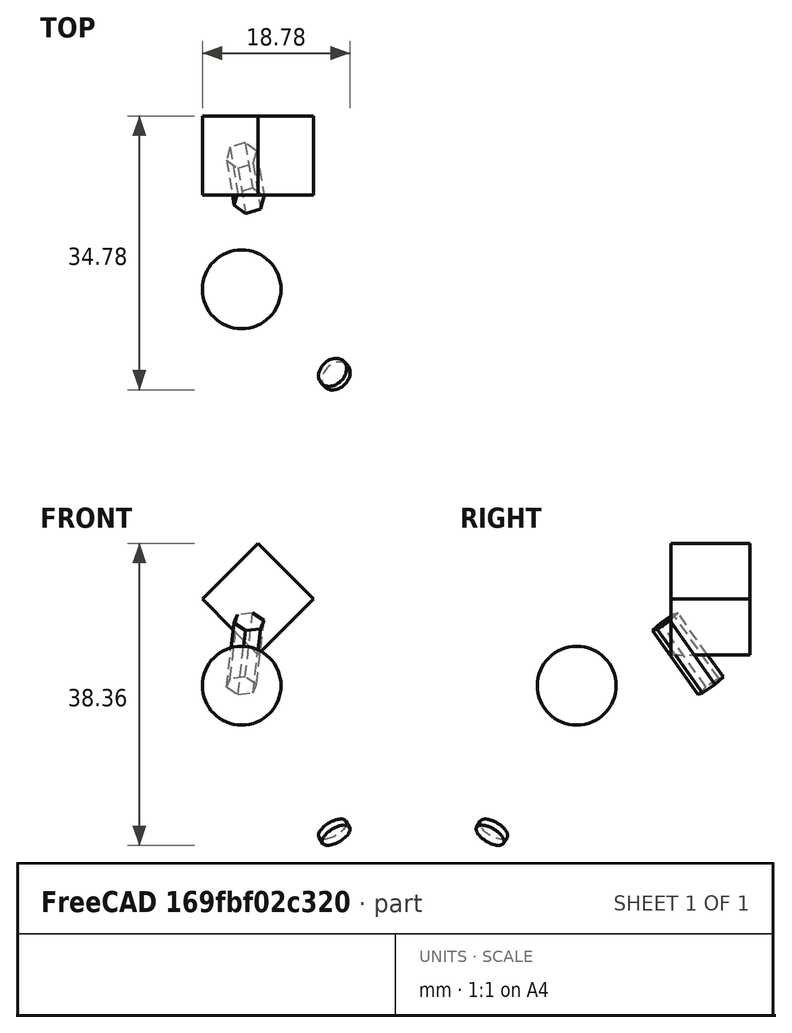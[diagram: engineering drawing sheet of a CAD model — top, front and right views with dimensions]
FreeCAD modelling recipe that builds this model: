
FCSTD DOCUMENT  (FreeCAD 1.1R44874 (Git))
Label: nested-structure
License: All rights reserved
LicenseURL: https://en.wikipedia.org/wiki/All_rights_reserved
objects: App::Point×6, App::LinkGroupPython×5, App::Part×5, App::Link×3, App::DocumentObjectGroup×3, Part::Box×1, Part::Sphere×1, Part::Cylinder×1, Part::FeaturePython×1, PartDesign::AdditivePrism×1, PartDesign::Body×1
note: 8 computed .brp shape members not serialized (recipe doc carries the construction recipe); baked Part::Feature solids carry a one-line shape summary decoded from their .brp
EXTERNAL_REF file=external-file.FCStd obj=Part
EXTERNAL_REF file=external-file.FCStd obj=Part002
EXTERNAL_REF file=external-file2.FCStd obj=Common

FEATURE [App::Link] Link001  label="external-file-mirror"
  LinkPlacement = pos=(0,0,23) rot=(0,1,0;0.785398rad)
  LinkedObject = -> <external external-file.FCStd>#Part
  Placement = pos=(0,0,23) rot=(0,1,0;0.785398rad)
  ShowElement = false
FEATURE [App::LinkGroupPython] OpticalPointSource  label="OpticalPointSource001"  # WARN: FeaturePython — macro-defined, semantics opaque (R4)
  Divergence = -
  FanPhi0 = 0
  Fans = 2
  FocalLength = -100
  LinkMode = 0
  MaxIntersectionsScale = 1
  MaxRayLengthScale = 1
  PhiDomain = 0, 2*pi
  PhiResolutionNumericMode = 100
  Placement = pos=(0,0,-5) rot=(0,0,1;0rad)
  PowerDensity = exp(-theta^2/0.01)
  RadiusDomain = 0, 1.00
  RadiusResolutionNumericMode = 100000
  RandomNumberGeneratorMode = ?
  RaysPerFan = 2000
  RaysPerIterationScale = 1
  RecordRays = false
  ThetaDomain = 0, 0.01
  ThetaResolutionNumericMode = 100000
  Wavelength = 500
FEATURE [Part::Box] Box  label="Cube"
  AttacherType = Attacher::AttachEngine3D
  Height = 10
  Length = 10
  Placement = pos=(-5,-5,11) rot=(0,1,0;0.785398rad)
  Width = 10
FEATURE [App::LinkGroupPython] OpticalMirrorGroup  # WARN: FeaturePython — macro-defined, semantics opaque (R4)
  AbsorptionLength = inf
  ElementList = -> [Box]
  GratingDiffractionOrder = 1
  GratingLinesOrientation = (0,0,1)
  GratingLinesPerMillimeter = 1000
  GratingType = 0
  LinkMode = 0
  ModifyPhiDomain = 0, 2*pi
  ModifyThetaDomain = -pi/2, pi/2
  OpticalType = 0
  Placement = pos=(1,0,-1) rot=(0,0,1;0rad)
  PowerPhiDomain = 0, 2*pi
  PowerThetaDomain = -pi/2, pi/2
  RecordHits = false
  Reflectivity = 1
  RefractiveIndex = 2
FEATURE [App::Link] Link  label="doubly-linked-lens"
  LinkedObject = -> <external external-file.FCStd>#Part002
FEATURE [App::Part] Part
  Group = -> [Link]
  Origin = -> Origin
  Placement = pos=(-17,0,11) rot=(0,0,1;0rad)
FEATURE [App::Point] Origin001
  Role = Origin
FEATURE [App::Link] Link002
  LinkedObject = -> <external external-file2.FCStd>#Common
FEATURE [App::Point] Origin003
  Role = Origin
FEATURE [App::Point] Origin005  label="Origin006"
  Role = Origin
FEATURE [App::Point] Origin007  label="Origin009"
  Role = Origin
FEATURE [App::Point] Origin009  label="Origin011"
  Role = Origin
FEATURE [App::Point] Origin011  label="Origin014"
  Role = Origin
FEATURE [Part::Sphere] Sphere
  Angle1 = -90
  Angle2 = 90
  Angle3 = 360
  AttacherType = Attacher::AttachEngine3D
  Placement = pos=(0,-17,0) rot=(0,0,1;0rad)
  Radius = 5
FEATURE [App::LinkGroupPython] OpticalLensGroup  # WARN: FeaturePython — macro-defined, semantics opaque (R4)
  AbsorptionLength = inf
  ElementList = -> [Link002,Sphere]
  GratingDiffractionOrder = 1
  GratingLinesOrientation = (0,0,1)
  GratingLinesPerMillimeter = 1000
  GratingType = 0
  LinkMode = 0
  ModifyPhiDomain = 0, 2*pi
  ModifyThetaDomain = -pi/2, pi/2
  OpticalType = 1
  PowerPhiDomain = 0, 2*pi
  PowerThetaDomain = -pi/2, pi/2
  RecordHits = false
  Reflectivity = 1
  RefractiveIndex = 1.2
FEATURE [Part::Cylinder] Cylinder
  Angle = 360
  AttacherType = Attacher::AttachEngine3D
  FirstAngle = 0
  Height = 1
  Placement = pos=(12,-28,-19) rot=(1,1,0;-0.698132rad)
  Radius = 2
  SecondAngle = 0
FEATURE [App::LinkGroupPython] OpticalVacuumGroup  label="OpticalAbsorberGroup"  # WARN: FeaturePython — macro-defined, semantics opaque (R4)
  AbsorptionLength = inf
  ElementList = -> [Cylinder]
  GratingDiffractionOrder = 1
  GratingLinesOrientation = (0,0,1)
  GratingLinesPerMillimeter = 1000
  GratingType = 0
  LinkMode = 0
  ModifyPhiDomain = 0, 2*pi
  ModifyThetaDomain = -pi/2, pi/2
  OpticalType = 3
  PowerPhiDomain = 0, 2*pi
  PowerThetaDomain = -pi/2, pi/2
  RecordHits = true
  Reflectivity = 1
  RefractiveIndex = 2
FEATURE [Part::FeaturePython] OpticalSimulationSettings  # WARN: FeaturePython — macro-defined, semantics opaque (R4)
  Active = true
  DistanceTolerance = 1e-06
  EnableStoreSingleShotData = false
  EndAfterHits = inf
  EndAfterIterations = inf
  EndAfterRays = 100
  MaxIntersections = 100
  MaxRayLength = 1000
  RaysPerIteration = 5
  SequentialMode = false
  ShowRaysInContinuousMode = true
  StoreHitFanIndex = false
  StoreHitInitDirection = false
  StoreHitInitPhi = false
  StoreHitInitPoint = false
  StoreHitInitPower = false
  StoreHitInitTheta = false
  StoreHitInitWavelength = false
  StoreHitRayIndex = false
  StoreHitTotalFanCount = false
  StoreHitTotalRaysInFan = false
  WorkerProcessCount = num_cpus
FEATURE [PartDesign::AdditivePrism] Prism001
  AttacherType = Attacher::AttachEngine3D
  Circumradius = 2
  FirstAngle = 0
  Height = 10
  Polygon = 6
  Refine = true
  SecondAngle = 0
  Suppressed = false
FEATURE [PartDesign::Body] Body
  AllowCompound = false
  Group = -> [Prism001]
  Origin = -> Origin002
  Placement = pos=(0,0,0) rot=(2,0,1;0.698132rad)
  Tip = -> Prism001
FEATURE [App::Part] Part001
  Group = -> [Body]
  Origin = -> Origin004
  Placement = pos=(7,-4,-6) rot=(-7,6,-5;0.20944rad)
FEATURE [App::LinkGroupPython] OpticalMirrorGroup001  # WARN: FeaturePython — macro-defined, semantics opaque (R4)
  AbsorptionLength = inf
  ElementList = -> [Part001]
  GratingDiffractionOrder = 1
  GratingLinesOrientation = (0,0,1)
  GratingLinesPerMillimeter = 1000
  GratingType = 0
  LinkMode = 0
  ModifyPhiDomain = 0, 2*pi
  ModifyThetaDomain = -pi/2, pi/2
  OpticalType = 0
  Placement = pos=(0,24,21) rot=(-3,3,1;-0.139626rad)
  PowerPhiDomain = 0, 2*pi
  PowerThetaDomain = -pi/2, pi/2
  RecordHits = false
  Reflectivity = 1
  RefractiveIndex = 2
FEATURE [App::Part] Part004
  Group = -> [OpticalMirrorGroup001]
  Origin = -> Origin010
  Placement = pos=(0,0,0) rot=(-3,1,2;-0.767945rad)
FEATURE [App::DocumentObjectGroup] Group002
  Group = -> [Part004]
FEATURE [App::DocumentObjectGroup] Group001
  Group = -> [Group002]
FEATURE [App::Part] Part003
  Group = -> [Group001,Part004,Group002]
  Origin = -> Origin008
  Placement = pos=(-9,8,6) rot=(0,-2,4;0.314159rad)
FEATURE [App::Part] Part002
  Group = -> [Part003]
  Origin = -> Origin006
  Placement = pos=(-12,-7,-6) rot=(3,1,0;0.069813rad)
FEATURE [App::DocumentObjectGroup] Group  label="deeply-nested"
  Group = -> [Part002]

RESOLVED EXTERNAL PARTS (link-assembly join: the EXTERNAL_REF files above that resolve inside this repo's crawl, each included once):
---- part external-file.FCStd = doc fcstd_b1e3236600b9 ----
FCSTD DOCUMENT  (FreeCAD 1.1R44874 (Git))
Label: external-file
License: All rights reserved
LicenseURL: https://en.wikipedia.org/wiki/All_rights_reserved
objects: App::Point×3, App::Part×3, Part::Cylinder×1, App::LinkGroupPython×1, App::Link×1
note: 1 computed .brp shape members not serialized (recipe doc carries the construction recipe); baked Part::Feature solids carry a one-line shape summary decoded from their .brp
EXTERNAL_REF file=external-file2.FCStd obj=Part

FEATURE [Part::Cylinder] Cylinder
  Angle = 360
  AttacherType = Attacher::AttachEngine3D
  FirstAngle = 0
  Height = 1
  Radius = 2
  SecondAngle = 0
FEATURE [App::LinkGroupPython] OpticalMirrorGroup  label="linkedMirrorGroup"  # WARN: FeaturePython — macro-defined, semantics opaque (R4)
  AbsorptionLength = inf
  ElementList = -> [Cylinder]
  GratingDiffractionOrder = 1
  GratingLinesOrientation = (0,0,1)
  GratingLinesPerMillimeter = 1000
  GratingType = 0
  LinkMode = 0
  ModifyPhiDomain = 0, 2*pi
  ModifyThetaDomain = -pi/2, pi/2
  OpticalType = 0
  PowerPhiDomain = 0, 2*pi
  PowerThetaDomain = -pi/2, pi/2
  RecordHits = false
  Reflectivity = 1
  RefractiveIndex = 2
FEATURE [App::Point] Origin001
  Role = Origin
FEATURE [App::Part] Part001
  Group = -> [OpticalMirrorGroup]
  Origin = -> Origin002
  Placement = pos=(0,0,-25) rot=(0,0,1;0rad)
FEATURE [App::Part] Part
  Group = -> [Part001]
  Origin = -> Origin
FEATURE [App::Point] Origin003
  Role = Origin
FEATURE [App::Point] Origin005  label="Origin006"
  Role = Origin
FEATURE [App::Link] Link
  LinkedObject = -> <external external-file2.FCStd>#Part
FEATURE [App::Part] Part002  label="link-lens"
  Group = -> [Link]
  Origin = -> Origin004
---- part external-file2.FCStd = doc fcstd_2f1645f87d6c ----
FCSTD DOCUMENT  (FreeCAD 1.1R44874 (Git))
Label: external-file2
License: All rights reserved
LicenseURL: https://en.wikipedia.org/wiki/All_rights_reserved
objects: Part::Sphere×2, Part::Cylinder×1, Part::MultiCommon×1, App::Point×1, App::LinkGroupPython×1, App::Part×1
note: 4 computed .brp shape members not serialized (recipe doc carries the construction recipe); baked Part::Feature solids carry a one-line shape summary decoded from their .brp

FEATURE [Part::Sphere] Sphere
  Angle1 = -90
  Angle2 = 90
  Angle3 = 360
  AttacherType = Attacher::AttachEngine3D
  Placement = pos=(0,0,-2) rot=(0,0,1;0rad)
  Radius = 5
FEATURE [Part::Sphere] Sphere001
  Angle1 = -90
  Angle2 = 90
  Angle3 = 360
  AttacherType = Attacher::AttachEngine3D
  Placement = pos=(0,0,7) rot=(0,0,1;0rad)
  Radius = 5
FEATURE [Part::Cylinder] Cylinder
  Angle = 360
  AttacherType = Attacher::AttachEngine3D
  FirstAngle = 0
  Height = 10
  Placement = pos=(0,0,-3) rot=(0,0,1;0rad)
  Radius = 2
  SecondAngle = 0
FEATURE [Part::MultiCommon] Common
  Behavior = 0
  Refine = true
  Shapes = -> [Sphere,Sphere001,Cylinder]
FEATURE [App::Point] Origin001
  Role = Origin
FEATURE [App::LinkGroupPython] OpticalLensGroup  # WARN: FeaturePython — macro-defined, semantics opaque (R4)
  AbsorptionLength = inf
  ElementList = -> [Common]
  GratingDiffractionOrder = 1
  GratingLinesOrientation = (0,0,1)
  GratingLinesPerMillimeter = 1000
  GratingType = 0
  LinkMode = 0
  ModifyPhiDomain = 0, 2*pi
  ModifyThetaDomain = -pi/2, pi/2
  OpticalType = 1
  Placement = pos=(0,0,-2.5) rot=(0,0,1;0rad)
  PowerPhiDomain = 0, 2*pi
  PowerThetaDomain = -pi/2, pi/2
  RecordHits = false
  Reflectivity = 1
  RefractiveIndex = 1.4
FEATURE [App::Part] Part  label="spherical-lens"
  Group = -> [OpticalLensGroup]
  Origin = -> Origin
